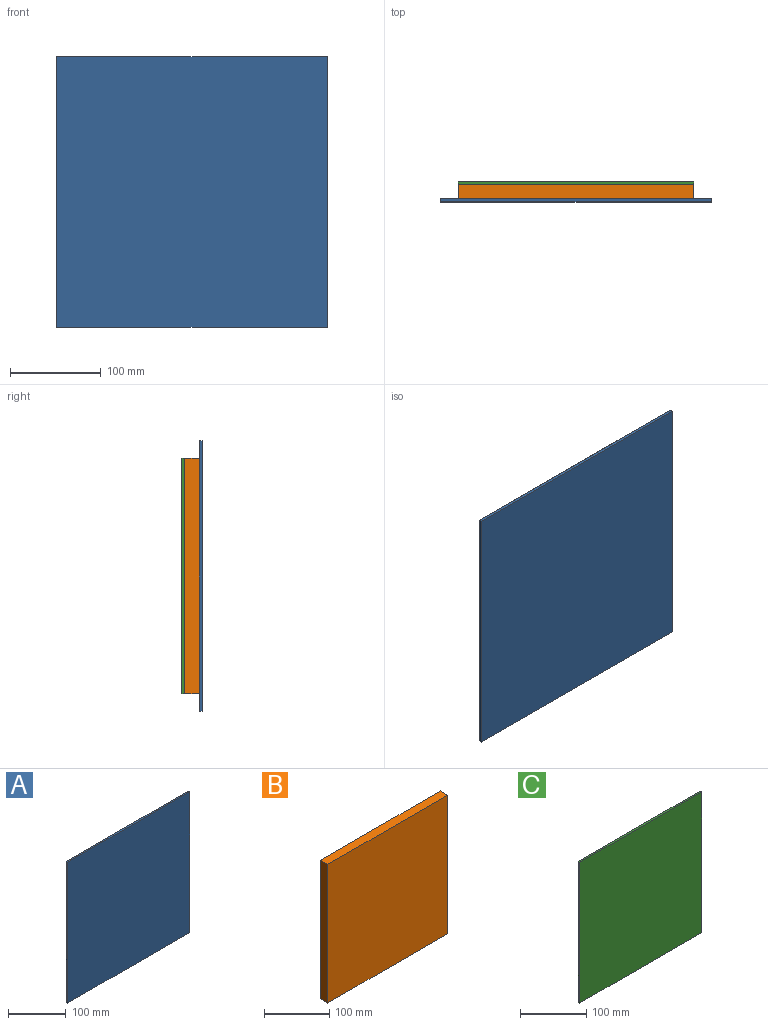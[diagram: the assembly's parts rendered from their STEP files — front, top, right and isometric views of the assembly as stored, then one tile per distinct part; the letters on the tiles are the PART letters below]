
ASSEMBLY  parts=3 mates=2
PART A: 6 faces, bbox 298.5x3.2x298.5 mm
  f0: plane 298.45x3.18mm, normal (0,0,-1), area 947.6mm2, adj f1,f3,f4,f5
  f1: plane 298.45x3.18mm, normal (1,0,0), area 947.6mm2, adj f0,f2,f4,f5
  f2: plane 298.45x3.18mm, normal (0,0,1), area 947.6mm2, adj f1,f3,f4,f5
  f3: plane 298.45x3.18mm, normal (-1,0,0), area 947.6mm2, adj f0,f2,f4,f5
  f4: plane 298.45x298.45mm, normal (0,-1,0), area 89072.4mm2, adj f0,f1,f2,f3
  f5: plane 298.45x298.45mm, normal (0,1,0), area 89072.4mm2, adj f0,f1,f2,f3
PART B: 6 faces, bbox 260.4x15.9x260.4 mm
  f0: plane 260.35x15.88mm, normal (0,0,-1), area 4133.1mm2, adj f1,f3,f4,f5
  f1: plane 260.35x15.88mm, normal (1,0,0), area 4133.1mm2, adj f0,f2,f4,f5
  f2: plane 260.35x15.88mm, normal (0,0,1), area 4133.1mm2, adj f1,f3,f4,f5
  f3: plane 260.35x15.88mm, normal (-1,0,0), area 4133.1mm2, adj f0,f2,f4,f5
  f4: plane 260.35x260.35mm, normal (0,-1,0), area 67782.1mm2, adj f0,f1,f2,f3
  f5: plane 260.35x260.35mm, normal (0,1,0), area 67782.1mm2, adj f0,f1,f2,f3
PART C: 6 faces, bbox 260.4x3.2x260.4 mm
  f0: plane 260.35x3.18mm, normal (0,0,-1), area 826.6mm2, adj f1,f3,f4,f5
  f1: plane 260.35x3.18mm, normal (1,0,0), area 826.6mm2, adj f0,f2,f4,f5
  f2: plane 260.35x3.18mm, normal (0,0,1), area 826.6mm2, adj f1,f3,f4,f5
  f3: plane 260.35x3.18mm, normal (-1,0,0), area 826.6mm2, adj f0,f2,f4,f5
  f4: plane 260.35x260.35mm, normal (0,-1,0), area 67782.1mm2, adj f0,f1,f2,f3
  f5: plane 260.35x260.35mm, normal (0,1,0), area 67782.1mm2, adj f0,f1,f2,f3
PLACE A t=(81.2,80.73,-881.11)mm
PLACE B t=(81.2,96.61,-881.11)mm
PLACE C t=(81.2,99.78,-881.11)mm
MATE fastened B.f5 <-> C.f4  axis (0,1,0) through (81.2,96.61,76.97)mm
MATE fastened A.f5 <-> B.f4  axis (0,1,0) through (81.2,80.73,76.97)mm
